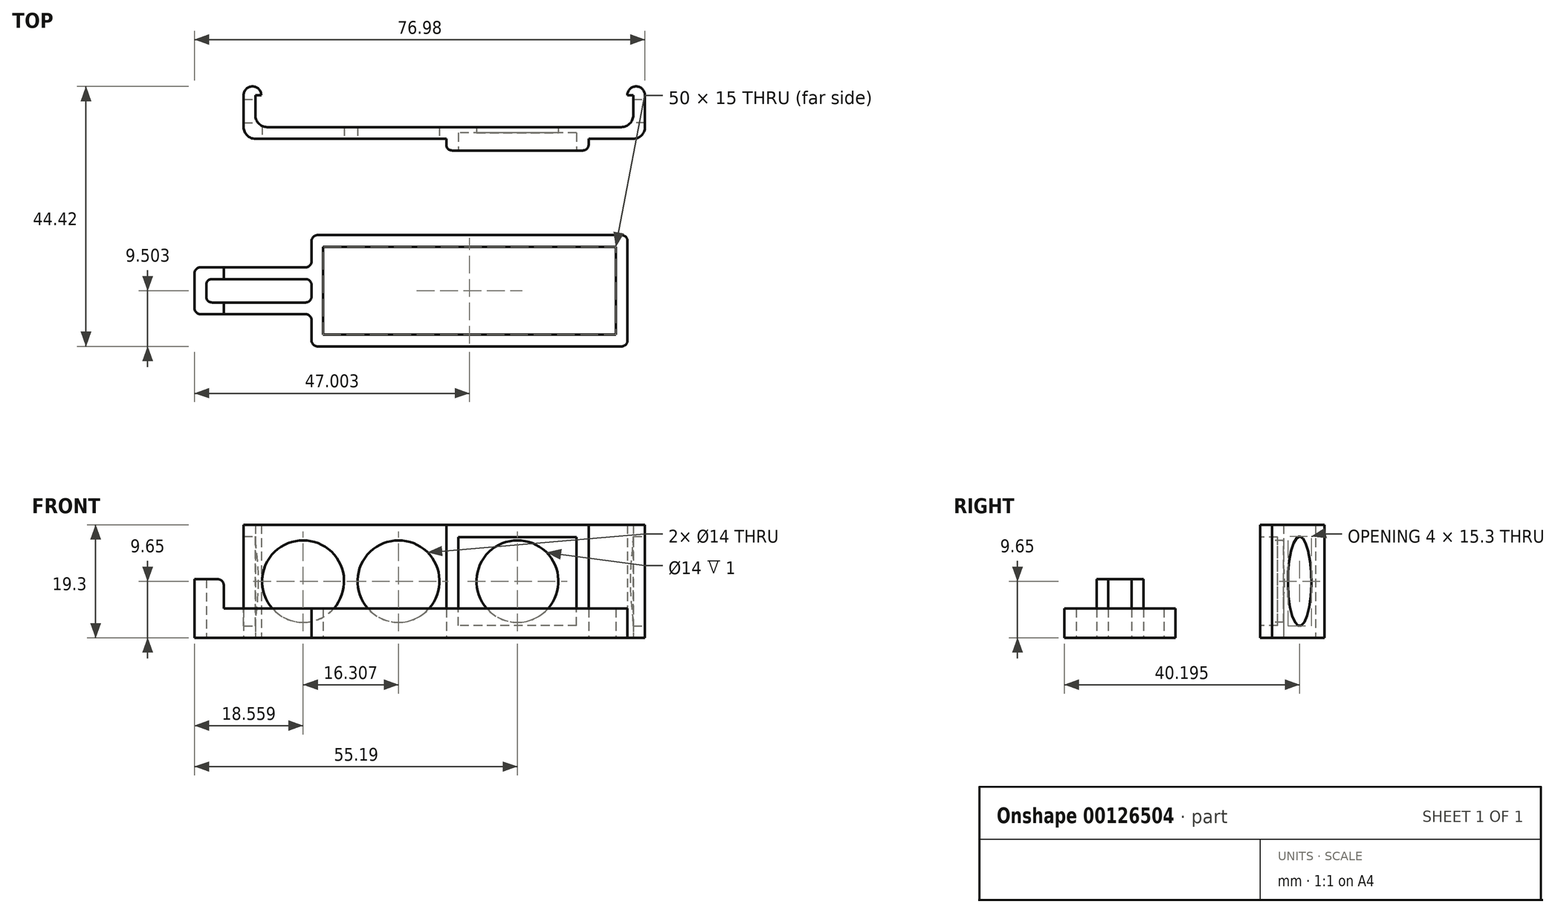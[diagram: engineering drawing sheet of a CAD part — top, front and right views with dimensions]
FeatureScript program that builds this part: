
annotation { "Feature Type Name" : "Feature", "Feature Type Description" : "" }
export const myFeature = defineFeature(function(context is Context, id is Id, definition is map)
    precondition{}
    {
        {
            assignVariable(context, id + "F0", {"name" : "Height", "anyValue" : 19.3});
        }
        {
            var Q0;
            Q0=qCreatedBy(makeId("Top.planeOp"),FACE);
            var sketch = newSketch(context, id + "F1", { "sketchPlane" : qUnion([Q0])});
            skLineSegment(sketch, "E0.bottom", {"start": v(32.28, -1) * mm, "end": v(24.67, -1) * mm});
            skLineSegment(sketch, "E0.top", {"start": v(30.29, 1) * mm, "end": v(-30.29, 1) * mm});
            skLineSegment(sketch, "E0.left", {"start": v(34.29, 1) * mm, "end": v(34.29, 1) * mm});
            skLineSegment(sketch, "E0.right", {"start": v(-34.28, 1) * mm, "end": v(-34.28, 1) * mm});
            skPoint(sketch, "E0.middle", {"position": v(0, 0) * mm});
            skLineSegment(sketch, "E1", {"start": v(0, 17.08) * mm, "end": v(0, -26.51) * mm, "construction": true});
            skLineSegment(sketch, "E2.left", {"start": v(-34.29, 1) * mm, "end": v(-34.29, 6.45) * mm});
            skLineSegment(sketch, "E2.right", {"start": v(-32.29, 3) * mm, "end": v(-32.29, 6.45) * mm});
            skLineSegment(sketch, "E3", {"start": v(-32.29, 6.45) * mm, "end": v(-31.29, 6.45) * mm});
            skArc(sketch, "E4", {"start": v(-34.29, 6.45) * mm, "mid": v(-32.79, 7.95) * mm, "end": v(-31.29, 6.45) * mm});
            skPoint(sketch, "E5.visualSharp", {"position": v(-32.29, 1) * mm});
            skArc(sketch, "E5.filletArc", {"start": v(-32.29, 3) * mm, "mid": v(-31.7, 1.59) * mm, "end": v(-30.29, 1) * mm});
            skPoint(sketch, "E6.visualSharp", {"position": v(-34.29, -1) * mm});
            skArc(sketch, "E6.filletArc", {"start": v(-34.29, 1) * mm, "mid": v(-33.7, -0.41) * mm, "end": v(-32.29, -1) * mm});
            skPoint(sketch, "E7.visualSharp", {"position": v(34.28, -1) * mm});
            skArc(sketch, "E7.filletArc", {"start": v(32.28, -1) * mm, "mid": v(33.7, -0.41) * mm, "end": v(34.28, 1) * mm});
            skLineSegment(sketch, "E8.MirrorCS", {"start": v(32.29, 6.45) * mm, "end": v(31.29, 6.45) * mm});
            skArc(sketch, "E9.MirrorCS", {"start": v(32.29, 3) * mm, "mid": v(31.7, 1.59) * mm, "end": v(30.29, 1) * mm});
            skLineSegment(sketch, "E10.MirrorCS", {"start": v(32.28, 3) * mm, "end": v(32.28, 6.45) * mm});
            skLineSegment(sketch, "E11.MirrorCS", {"start": v(34.28, 1) * mm, "end": v(34.28, 6.45) * mm});
            skArc(sketch, "E12.MirrorCS", {"start": v(34.29, 6.45) * mm, "mid": v(32.79, 7.95) * mm, "end": v(31.29, 6.45) * mm});
            skLineSegment(sketch, "E13.bottom", {"start": v(12.17, 1) * mm, "end": v(-12.17, 1) * mm});
            skPoint(sketch, "E13.middle", {"position": v(0, -1) * mm});
            skLineSegment(sketch, "E14.trimOffspring", {"start": v(-12.17, -1) * mm, "end": v(-32.29, -1) * mm});
            skLineSegment(sketch, "E15", {"start": v(12.5, 17.08) * mm, "end": v(12.5, -1) * mm, "construction": true});
            skLineSegment(sketch, "E16", {"start": v(-12.17, -1) * mm, "end": v(0.33, -1) * mm});
            skPoint(sketch, "E17.orphan", {"position": v(-12.17, -3) * mm});
            skPoint(sketch, "E13.left.end.orphan", {"position": v(12.17, -3) * mm});
            skPoint(sketch, "E18.orphan", {"position": v(12.5, -26.51) * mm});
            skLineSegment(sketch, "E19.bottom", {"start": v(24.67, 1) * mm, "end": v(0.33, 1) * mm});
            skLineSegment(sketch, "E19.top", {"start": v(24.67, -3) * mm, "end": v(0.33, -3) * mm});
            skLineSegment(sketch, "E19.left", {"start": v(24.67, 1) * mm, "end": v(24.67, -3) * mm});
            skLineSegment(sketch, "E19.right", {"start": v(0.33, 1) * mm, "end": v(0.33, -3) * mm});
            skPoint(sketch, "E19.middle", {"position": v(12.5, -1) * mm});
            skSolve(sketch);
        }
        {
            var Q0;
            Q0 = qSketchRegion(id + "F1", true);
            extrude(context, id + "F2", {"entities" : qUnion([Q0]), "depth" : (getVariable(context, 'Height')) * mm});
        }
        {
            var Q0;
            Q0=makeQuery(id+"F2.opExtrude","SWEPT_FACE",FACE,{"disambiguationData":[OSD([sQuery(id+"F1.wireOp",EDGE,"E19.top")])]});
            var sketch = newSketch(context, id + "F3", { "sketchPlane" : qUnion([Q0])});
            skLineSegment(sketch, "E20", {"start": v(12.5, 19.3) * mm, "end": v(12.5, 0) * mm, "construction": true});
            skLineSegment(sketch, "E21.bottom", {"start": v(22.6, 2.07) * mm, "end": v(2.4, 2.07) * mm});
            skLineSegment(sketch, "E21.top", {"start": v(22.6, 17.23) * mm, "end": v(2.4, 17.23) * mm});
            skLineSegment(sketch, "E21.left", {"start": v(22.6, 2.07) * mm, "end": v(22.6, 17.23) * mm});
            skLineSegment(sketch, "E21.right", {"start": v(2.4, 2.07) * mm, "end": v(2.4, 17.23) * mm});
            skPoint(sketch, "E21.middle", {"position": v(12.5, 9.65) * mm});
            skSolve(sketch);
        }
        {
            var Q0;
            Q0=makeQuery(id+"F2.opExtrude","SWEPT_FACE",FACE,{"disambiguationData":[OSD([sQuery(id+"F1.wireOp",EDGE,"E11.MirrorCS")])]});
            var sketch = newSketch(context, id + "F4", { "sketchPlane" : qUnion([Q0])});
            skEllipse(sketch, "E22", {"center": v(3.73, 9.65) * mm, "majorRadius": 7.65 * mm, "minorRadius": 2 * mm, "majorAxis": v(0, 1)});
            skPoint(sketch, "E22.centerSnap0", {"position": v(3.73, 19.3) * mm});
            skPoint(sketch, "E22.centerSnap1", {"position": v(1, 9.65) * mm});
            skSolve(sketch);
        }
        {
            var Q0;
            Q0=makeQuery(id+"F4.imprint","IMPRINT",FACE,{"disambiguationData":[TD([[makeQuery(id+"F4.imprint","IMPRINT",EDGE,{"derivedFrom":sQuery(id+"F4.wireOp",EDGE,"E22")}),1.0]])]});
            extrude(context, id + "F5", {"entities" : qUnion([Q0]), "operationType" : NewBodyOperationType.REMOVE, "endBound" : BoundingType.THROUGH_ALL, "oppositeDirection" : true, "depth" : 25 * mm});
        }
        {
            var Q0;
            Q0=qCreatedBy(makeId("Top.planeOp"),FACE);
            var sketch = newSketch(context, id + "F6", { "sketchPlane" : qUnion([Q0])});
            skLineSegment(sketch, "E23.bottom", {"start": v(-20.69, -19.47) * mm, "end": v(29.31, -19.47) * mm});
            skLineSegment(sketch, "E23.top", {"start": v(-20.69, -34.47) * mm, "end": v(29.31, -34.47) * mm});
            skLineSegment(sketch, "E23.left", {"start": v(-20.69, -19.47) * mm, "end": v(-20.69, -34.47) * mm});
            skLineSegment(sketch, "E23.right", {"start": v(29.31, -19.47) * mm, "end": v(29.31, -34.47) * mm});
            skLineSegment(sketch, "E24.bottom", {"start": v(-22.69, -36.47) * mm, "end": v(31.31, -36.47) * mm});
            skLineSegment(sketch, "E24.top", {"start": v(-22.69, -17.47) * mm, "end": v(31.31, -17.47) * mm});
            skLineSegment(sketch, "E24.left", {"start": v(-22.69, -36.47) * mm, "end": v(-22.69, -30.97) * mm});
            skLineSegment(sketch, "E24.right", {"start": v(31.31, -36.47) * mm, "end": v(31.31, -17.47) * mm});
            skPoint(sketch, "E24.middle", {"position": v(4.31, -26.97) * mm});
            skPoint(sketch, "E24.middle.positionSnap0", {"position": v(-20.69, -26.97) * mm});
            skPoint(sketch, "E24.middle.positionSnap1", {"position": v(4.31, -34.47) * mm});
            skPoint(sketch, "E24.centerSnap0", {"position": v(-20.69, -26.97) * mm});
            skPoint(sketch, "E24.centerSnap1", {"position": v(4.31, -34.47) * mm});
            skLineSegment(sketch, "E25.bottom", {"start": v(-22.69, -22.97) * mm, "end": v(-42.69, -22.97) * mm});
            skLineSegment(sketch, "E25.top", {"start": v(-22.69, -30.97) * mm, "end": v(-42.69, -30.97) * mm});
            skLineSegment(sketch, "E25.right", {"start": v(-42.69, -22.97) * mm, "end": v(-42.69, -30.97) * mm});
            skLineSegment(sketch, "E26.trimOffspring", {"start": v(-22.69, -22.97) * mm, "end": v(-22.69, -17.47) * mm});
            skLineSegment(sketch, "E27", {"start": v(-22.69, -28.97) * mm, "end": v(-22.69, -24.97) * mm});
            skLineSegment(sketch, "E28.bottom", {"start": v(-22.69, -24.97) * mm, "end": v(-40.69, -24.97) * mm});
            skLineSegment(sketch, "E28.top", {"start": v(-22.69, -28.97) * mm, "end": v(-40.69, -28.97) * mm});
            skLineSegment(sketch, "E28.left", {"start": v(-22.69, -24.97) * mm, "end": v(-22.69, -28.97) * mm});
            skLineSegment(sketch, "E28.right", {"start": v(-40.69, -24.97) * mm, "end": v(-40.69, -28.97) * mm});
            skSolve(sketch);
        }
        {
            var Q0;
            Q0=makeQuery(id+"F2.opExtrude","SWEPT_EDGE",EDGE,{"disambiguationData":[OSD([sQuery(id+"F1.wireOp",EDGE,"E19.top"),sQuery(id+"F1.wireOp",EDGE,"E19.right")])]});
            var Q1;
            Q1=makeQuery(id+"F2.opExtrude","SWEPT_EDGE",EDGE,{"disambiguationData":[OSD([sQuery(id+"F1.wireOp",EDGE,"E19.top"),sQuery(id+"F1.wireOp",EDGE,"E19.left")])]});
            fillet(context, id + "F7", {"entities" : qUnion([Q0, Q1]), "radius" : 1 * mm, "tangentPropagation" : true, "allowEdgeOverflow" : false});
        }
        {
            var Q0;
            Q0=makeQuery(id+"F6.imprint","IMPRINT",FACE,{"disambiguationData":[TD([[makeQuery(id+"F6.imprint","IMPRINT",EDGE,{"derivedFrom":sQuery(id+"F6.wireOp",EDGE,"E23.bottom")}),1.0]])]});
            extrude(context, id + "F8", {"entities" : qUnion([Q0]), "depth" : 5 * mm});
        }
        {
            var Q0;
            Q0=makeQuery(id+"F8.opExtrude","CAP_FACE",FACE,{"disambiguationData":[OSD([sQuery(id+"F6.wireOp",EDGE,"E23.bottom"),sQuery(id+"F6.wireOp",EDGE,"E23.top"),sQuery(id+"F6.wireOp",EDGE,"E23.left"),sQuery(id+"F6.wireOp",EDGE,"E23.right"),sQuery(id+"F6.wireOp",EDGE,"E24.bottom"),sQuery(id+"F6.wireOp",EDGE,"E24.top"),sQuery(id+"F6.wireOp",EDGE,"E24.left"),sQuery(id+"F6.wireOp",EDGE,"E24.right"),sQuery(id+"F6.wireOp",EDGE,"E25.bottom"),sQuery(id+"F6.wireOp",EDGE,"E25.top"),sQuery(id+"F6.wireOp",EDGE,"E25.right"),sQuery(id+"F6.wireOp",EDGE,"E26.trimOffspring"),sQuery(id+"F6.wireOp",EDGE,"E28.bottom"),sQuery(id+"F6.wireOp",EDGE,"E28.top"),sQuery(id+"F6.wireOp",EDGE,"E28.left"),sQuery(id+"F6.wireOp",EDGE,"E28.right")])],"isStart":false});
            var sketch = newSketch(context, id + "F9", { "sketchPlane" : qUnion([Q0])});
            skLineSegment(sketch, "E29.bottom", {"start": v(-42.69, -22.97) * mm, "end": v(-37.69, -22.97) * mm});
            skLineSegment(sketch, "E29.top", {"start": v(-42.69, -30.97) * mm, "end": v(-37.69, -30.97) * mm});
            skLineSegment(sketch, "E29.left", {"start": v(-42.69, -22.97) * mm, "end": v(-42.69, -30.97) * mm});
            skLineSegment(sketch, "E29.right", {"start": v(-37.69, -22.97) * mm, "end": v(-37.69, -30.97) * mm});
            skSolve(sketch);
        }
        {
            var Q0;
            {var subQ1=sQuery(id+"F9.wireOp",EDGE,"E29.bottom");Q0=makeQuery(id+"F9.imprint","IMPRINT",FACE,{"disambiguationData":[TD([[makeQuery(id+"F9.imprint","IMPRINT",EDGE,{"derivedFrom":subQ1}),1.0]])]});}
            extrude(context, id + "F10", {"entities" : qUnion([Q0]), "operationType" : NewBodyOperationType.ADD, "depth" : 5 * mm});
        }
        {
            var Q0;
            {var subQ0=sQuery(id+"F9.wireOp",EDGE,"E29.right");Q0=makeQuery(id+"F10.opExtrude","CAP_EDGE",EDGE,{"disambiguationData":[OSD([subQ0]),TDD([makeQuery(id+"F9.imprint","IMPRINT",EDGE,{"disambiguationData":[TD([[makeQuery(id+"F9.imprint","INTERSECT",VERTEX,{"derivedFrom":[makeQuery(id+"F8.opExtrude","CAP_EDGE",EDGE,{"disambiguationData":[OSD([sQuery(id+"F6.wireOp",EDGE,"E28.top")])],"isStart":false}),subQ0]}),-1.0]])],"derivedFrom":subQ0})])],"isStart":false});}
            var Q1;
            {var subQ0=sQuery(id+"F9.wireOp",EDGE,"E29.right");Q1=makeQuery(id+"F10.opExtrude","CAP_EDGE",EDGE,{"disambiguationData":[OSD([subQ0]),TDD([makeQuery(id+"F9.imprint","IMPRINT",EDGE,{"disambiguationData":[TD([[makeQuery(id+"F9.imprint","INTERSECT",VERTEX,{"derivedFrom":[makeQuery(id+"F8.opExtrude","CAP_EDGE",EDGE,{"disambiguationData":[OSD([sQuery(id+"F6.wireOp",EDGE,"E28.bottom")])],"isStart":false}),subQ0]}),1.0]])],"derivedFrom":subQ0})])],"isStart":false});}
            var Q2;
            Q2=makeQuery(id+"F8.opExtrude","SWEPT_EDGE",EDGE,{"disambiguationData":[OSD([sQuery(id+"F6.wireOp",EDGE,"E24.bottom"),sQuery(id+"F6.wireOp",EDGE,"E24.left")])]});
            var Q3;
            Q3=makeQuery(id+"F8.opExtrude","SWEPT_EDGE",EDGE,{"disambiguationData":[OSD([sQuery(id+"F6.wireOp",EDGE,"E24.bottom"),sQuery(id+"F6.wireOp",EDGE,"E24.right")])]});
            var Q4;
            Q4=makeQuery(id+"F8.opExtrude","SWEPT_EDGE",EDGE,{"disambiguationData":[OSD([sQuery(id+"F6.wireOp",EDGE,"E24.top"),sQuery(id+"F6.wireOp",EDGE,"E24.right")])]});
            var Q5;
            Q5=makeQuery(id+"F10.boolean.opBoolean","MERGE",EDGE,{"derivedFrom":[makeQuery(id+"F8.opExtrude","SWEPT_EDGE",EDGE,{"disambiguationData":[OSD([sQuery(id+"F6.wireOp",EDGE,"E25.top"),sQuery(id+"F6.wireOp",EDGE,"E25.right")])]}),makeQuery(id+"F10.opExtrude","SWEPT_EDGE",EDGE,{"disambiguationData":[OSD([sQuery(id+"F9.wireOp",EDGE,"E29.top"),sQuery(id+"F9.wireOp",EDGE,"E29.left")])]})]});
            var Q6;
            Q6=makeQuery(id+"F10.boolean.opBoolean","MERGE",EDGE,{"derivedFrom":[makeQuery(id+"F8.opExtrude","SWEPT_EDGE",EDGE,{"disambiguationData":[OSD([sQuery(id+"F6.wireOp",EDGE,"E25.bottom"),sQuery(id+"F6.wireOp",EDGE,"E25.right")])]}),makeQuery(id+"F10.opExtrude","SWEPT_EDGE",EDGE,{"disambiguationData":[OSD([sQuery(id+"F9.wireOp",EDGE,"E29.bottom"),sQuery(id+"F9.wireOp",EDGE,"E29.left")])]})]});
            var Q7;
            Q7=makeQuery(id+"F8.opExtrude","SWEPT_EDGE",EDGE,{"disambiguationData":[OSD([sQuery(id+"F6.wireOp",EDGE,"E25.bottom"),sQuery(id+"F6.wireOp",EDGE,"E26.trimOffspring")])]});
            var Q8;
            Q8=makeQuery(id+"F8.opExtrude","SWEPT_EDGE",EDGE,{"disambiguationData":[OSD([sQuery(id+"F6.wireOp",EDGE,"E24.top"),sQuery(id+"F6.wireOp",EDGE,"E26.trimOffspring")])]});
            var Q9;
            Q9=makeQuery(id+"F8.opExtrude","SWEPT_EDGE",EDGE,{"disambiguationData":[OSD([sQuery(id+"F6.wireOp",EDGE,"E24.left"),sQuery(id+"F6.wireOp",EDGE,"E25.top")])]});
            var Q10;
            {var subQ0=sQuery(id+"F6.wireOp",EDGE,"E28.right");var subQ1=sQuery(id+"F6.wireOp",EDGE,"E28.bottom");Q10=makeQuery(id+"F10.boolean.opBoolean","MERGE",EDGE,{"derivedFrom":[makeQuery(id+"F8.opExtrude","SWEPT_EDGE",EDGE,{"disambiguationData":[OSD([subQ1,subQ0])]}),makeQuery(id+"F10.opExtrude","SWEPT_EDGE",EDGE,{"disambiguationData":[OSD([subQ1,subQ0])]})]});}
            var Q11;
            {var subQ0=sQuery(id+"F6.wireOp",EDGE,"E28.right");var subQ1=sQuery(id+"F6.wireOp",EDGE,"E28.top");Q11=makeQuery(id+"F10.boolean.opBoolean","MERGE",EDGE,{"derivedFrom":[makeQuery(id+"F8.opExtrude","SWEPT_EDGE",EDGE,{"disambiguationData":[OSD([subQ1,subQ0])]}),makeQuery(id+"F10.opExtrude","SWEPT_EDGE",EDGE,{"disambiguationData":[OSD([subQ1,subQ0])]})]});}
            var Q12;
            Q12=makeQuery(id+"F8.opExtrude","SWEPT_EDGE",EDGE,{"disambiguationData":[OSD([sQuery(id+"F6.wireOp",EDGE,"E28.bottom"),sQuery(id+"F6.wireOp",EDGE,"E28.left")])]});
            var Q13;
            Q13=makeQuery(id+"F8.opExtrude","SWEPT_EDGE",EDGE,{"disambiguationData":[OSD([sQuery(id+"F6.wireOp",EDGE,"E28.top"),sQuery(id+"F6.wireOp",EDGE,"E28.left")])]});
            fillet(context, id + "F11", {"entities" : qUnion([Q0, Q1, Q2, Q3, Q4, Q5, Q6, Q7, Q8, Q9, Q10, Q11, Q12, Q13]), "radius" : 1 * mm, "tangentPropagation" : true, "allowEdgeOverflow" : false});
        }
        {
            var Q0;
            Q0=makeQuery(id+"F3.imprint","IMPRINT",FACE,{"disambiguationData":[TD([[makeQuery(id+"F3.imprint","IMPRINT",EDGE,{"derivedFrom":sQuery(id+"F3.wireOp",EDGE,"E21.bottom")}),-1.0]])]});
            extrude(context, id + "F12", {"entities" : qUnion([Q0]), "operationType" : NewBodyOperationType.REMOVE, "oppositeDirection" : true, "depth" : 3 * mm});
        }
        {
            var Q0;
            Q0=makeQuery(id+"F2.opExtrude","SWEPT_FACE",FACE,{"disambiguationData":[OSD([sQuery(id+"F1.wireOp",EDGE,"E14.trimOffspring"),sQuery(id+"F1.wireOp",EDGE,"E16")])]});
            var sketch = newSketch(context, id + "F13", { "sketchPlane" : qUnion([Q0])});
            skLineSegment(sketch, "E30", {"start": v(-15.98, 19.3) * mm, "end": v(-15.98, 0) * mm, "construction": true});
            skLineSegment(sketch, "E31", {"start": v(-32.29, 9.65) * mm, "end": v(0.33, 9.65) * mm, "construction": true});
            skLineSegment(sketch, "E32", {"start": v(-15.98, 19.3) * mm, "end": v(-32.29, 0) * mm, "construction": true});
            skLineSegment(sketch, "E33", {"start": v(-15.98, 19.3) * mm, "end": v(0.33, 0) * mm, "construction": true});
            skCircle(sketch, "E34", {"center": v(-24.13, 9.65) * mm, "radius": 7 * mm});
            skCircle(sketch, "E35", {"center": v(-7.82, 9.65) * mm, "radius": 7 * mm});
            skSolve(sketch);
        }
        {
            var Q0;
            Q0=makeQuery(id+"F12.boolean.opBoolean","COPY",FACE,{"derivedFrom":makeQuery(id+"F12.opExtrude","CAP_FACE",FACE,{"disambiguationData":[OSD([sQuery(id+"F3.wireOp",EDGE,"E21.bottom"),sQuery(id+"F3.wireOp",EDGE,"E21.top"),sQuery(id+"F3.wireOp",EDGE,"E21.left"),sQuery(id+"F3.wireOp",EDGE,"E21.right")])],"isStart":false})});
            var sketch = newSketch(context, id + "F14", { "sketchPlane" : qUnion([Q0])});
            skLineSegment(sketch, "E36", {"start": v(2.4, 17.23) * mm, "end": v(22.6, 2.07) * mm, "construction": true});
            skLineSegment(sketch, "E37", {"start": v(2.4, 2.07) * mm, "end": v(22.6, 17.23) * mm, "construction": true});
            skCircle(sketch, "E38", {"center": v(12.5, 9.65) * mm, "radius": 7 * mm});
            skSolve(sketch);
        }
        {
            var Q0;
            Q0=makeQuery(id+"F13.imprint","IMPRINT",FACE,{"disambiguationData":[TD([[makeQuery(id+"F13.imprint","IMPRINT",EDGE,{"derivedFrom":sQuery(id+"F13.wireOp",EDGE,"E34")}),1.0]])]});
            var Q1;
            Q1=makeQuery(id+"F13.imprint","IMPRINT",FACE,{"disambiguationData":[TD([[makeQuery(id+"F13.imprint","IMPRINT",EDGE,{"derivedFrom":sQuery(id+"F13.wireOp",EDGE,"E35")}),1.0]])]});
            var Q2;
            Q2=makeQuery(id+"F14.imprint","IMPRINT",FACE,{"disambiguationData":[TD([[makeQuery(id+"F14.imprint","IMPRINT",EDGE,{"derivedFrom":sQuery(id+"F14.wireOp",EDGE,"E38")}),1.0]])]});
            extrude(context, id + "F15", {"entities" : qUnion([Q0, Q1, Q2]), "operationType" : NewBodyOperationType.REMOVE, "endBound" : BoundingType.THROUGH_ALL, "oppositeDirection" : true, "depth" : 25 * mm});
        }
    });
